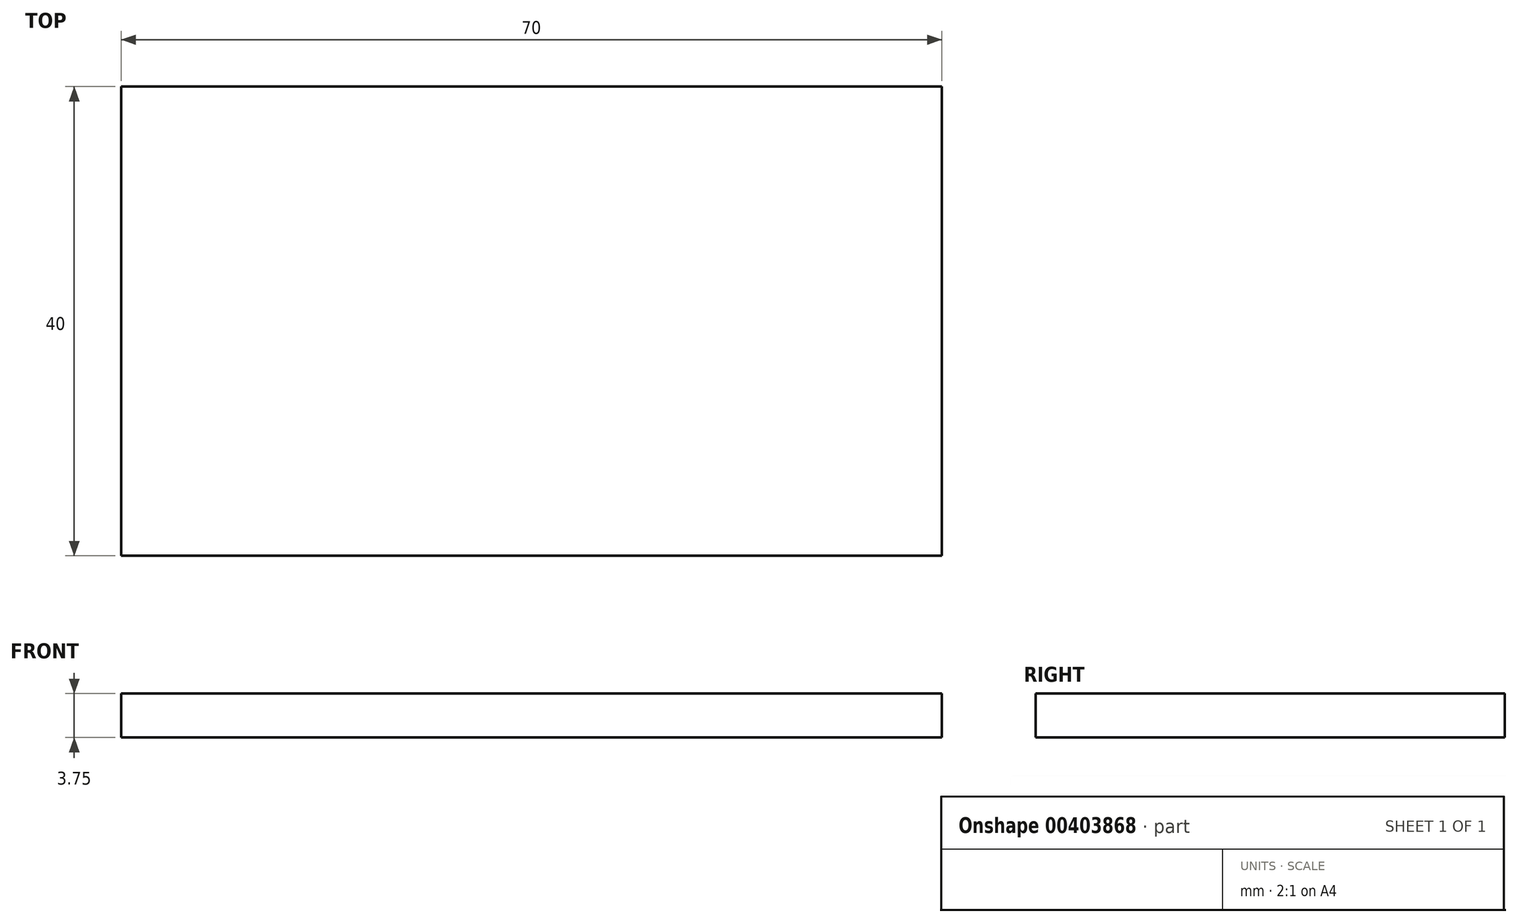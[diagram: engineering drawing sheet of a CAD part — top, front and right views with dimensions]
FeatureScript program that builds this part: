
annotation { "Feature Type Name" : "Feature", "Feature Type Description" : "" }
export const myFeature = defineFeature(function(context is Context, id is Id, definition is map)
    precondition{}
    {
        {
            var Q0;
            Q0=qCreatedBy(makeId("Top.planeOp"),FACE);
            var sketch = newSketch(context, id + "F0", { "sketchPlane" : qUnion([Q0])});
            skLineSegment(sketch, "E0.bottom", {"start": v(35, 20) * mm, "end": v(-35, 20) * mm});
            skLineSegment(sketch, "E0.top", {"start": v(35, -20) * mm, "end": v(-35, -20) * mm});
            skLineSegment(sketch, "E0.left", {"start": v(35, 20) * mm, "end": v(35, -20) * mm});
            skLineSegment(sketch, "E0.right", {"start": v(-35, 20) * mm, "end": v(-35, -20) * mm});
            skPoint(sketch, "E0.middle", {"position": v(0, 0) * mm});
            skSolve(sketch);
        }
        {
            var Q0;
            Q0 = qSketchRegion(id + "F0", true);
            extrude(context, id + "F1", {"entities" : qUnion([Q0]), "depth" : 3.75 * mm});
        }
    });
